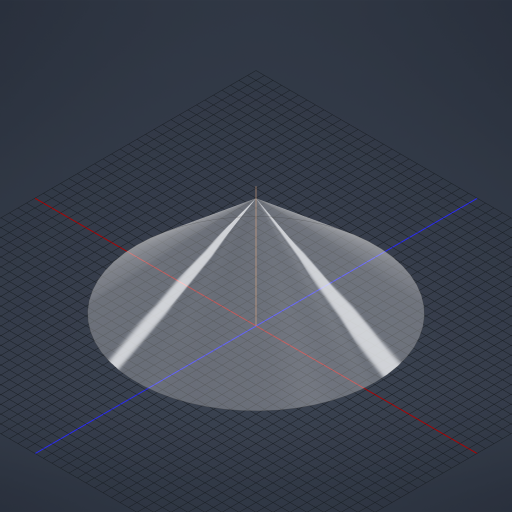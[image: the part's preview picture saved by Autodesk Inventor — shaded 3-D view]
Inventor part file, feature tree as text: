
AUTODESK INVENTOR PART (.ipt)
format: ipt  version: 2023.2 (Build 272271030, 271C)  size: 304,128 bytes
history: native  units: mm
features: revolve x1, other x1, sketch x1
ambient origin geometry x8: Origin, YZ Plane, XZ Plane, XY Plane, X Axis, Y Axis, Z Axis, Center Point
bodies: Volumenkörper1 (feature_tree)
feature tree (3):
  revolve  "Umdrehung1"
  other  "Arbeitsachse1"
  sketch  "Skizze6"  dims[d3=8.726646mm d4=360.0deg d6=470.0mm]
